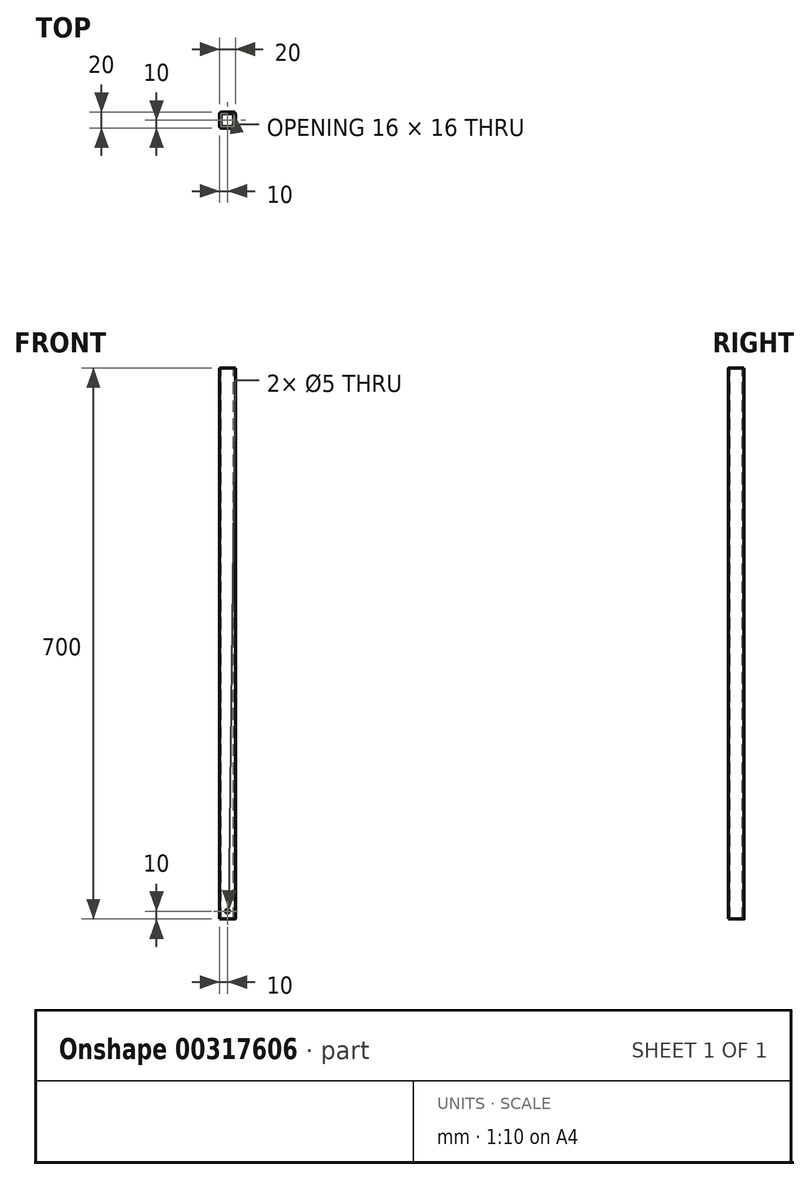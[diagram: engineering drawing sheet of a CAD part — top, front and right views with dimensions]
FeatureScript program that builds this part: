
annotation { "Feature Type Name" : "Feature", "Feature Type Description" : "" }
export const myFeature = defineFeature(function(context is Context, id is Id, definition is map)
    precondition{}
    {
        {
            var Q0;
            Q0=qCreatedBy(makeId("Top.planeOp"),FACE);
            var sketch = newSketch(context, id + "F0", { "sketchPlane" : qUnion([Q0])});
            skLineSegment(sketch, "E0.bottom", {"start": v(10, -10) * mm, "end": v(-10, -10) * mm});
            skLineSegment(sketch, "E0.top", {"start": v(10, 10) * mm, "end": v(-10, 10) * mm});
            skLineSegment(sketch, "E0.left", {"start": v(10, -10) * mm, "end": v(10, 10) * mm});
            skLineSegment(sketch, "E0.right", {"start": v(-10, -10) * mm, "end": v(-10, 10) * mm});
            skSolve(sketch);
        }
        {
            var Q0;
            Q0=makeQuery(id+"F0.imprint","IMPRINT",FACE,{"disambiguationData":[TD([[makeQuery(id+"F0.imprint","IMPRINT",EDGE,{"derivedFrom":sQuery(id+"F0.wireOp",EDGE,"E0.bottom")}),-1.0]])]});
            extrude(context, id + "F1", {"entities" : qUnion([Q0]), "depth" : 700 * mm});
        }
        {
            var Q0;
            Q0=makeQuery(id+"F1.opExtrude","SWEPT_EDGE",EDGE,{"disambiguationData":[OSD([sQuery(id+"F0.wireOp",EDGE,"E0.top"),sQuery(id+"F0.wireOp",EDGE,"E0.right")])]});
            var Q1;
            Q1=makeQuery(id+"F1.opExtrude","SWEPT_EDGE",EDGE,{"disambiguationData":[OSD([sQuery(id+"F0.wireOp",EDGE,"E0.bottom"),sQuery(id+"F0.wireOp",EDGE,"E0.right")])]});
            var Q2;
            Q2=makeQuery(id+"F1.opExtrude","SWEPT_EDGE",EDGE,{"disambiguationData":[OSD([sQuery(id+"F0.wireOp",EDGE,"E0.bottom"),sQuery(id+"F0.wireOp",EDGE,"E0.left")])]});
            var Q3;
            Q3=makeQuery(id+"F1.opExtrude","SWEPT_EDGE",EDGE,{"disambiguationData":[OSD([sQuery(id+"F0.wireOp",EDGE,"E0.top"),sQuery(id+"F0.wireOp",EDGE,"E0.left")])]});
            fillet(context, id + "F2", {"entities" : qUnion([Q0, Q1, Q2, Q3]), "radius" : 2 * mm, "tangentPropagation" : true, "allowEdgeOverflow" : false});
        }
        {
            var Q0;
            Q0=makeQuery(id+"F1.opExtrude","CAP_FACE",FACE,{"disambiguationData":[OSD([sQuery(id+"F0.wireOp",EDGE,"E0.bottom"),sQuery(id+"F0.wireOp",EDGE,"E0.top"),sQuery(id+"F0.wireOp",EDGE,"E0.left"),sQuery(id+"F0.wireOp",EDGE,"E0.right")])],"isStart":false});
            var Q1;
            Q1=makeQuery(id+"F1.opExtrude","CAP_FACE",FACE,{"disambiguationData":[OSD([sQuery(id+"F0.wireOp",EDGE,"E0.bottom"),sQuery(id+"F0.wireOp",EDGE,"E0.top"),sQuery(id+"F0.wireOp",EDGE,"E0.left"),sQuery(id+"F0.wireOp",EDGE,"E0.right")])],"isStart":true});
            shell(context, id + "F3", {"entities" : qUnion([Q0, Q1]), "thickness" : 2 * mm});
        }
        {
            var Q0;
            Q0=makeQuery(id+"F3.opShell","OFFSET_EDGE",EDGE,{"disambiguationData":[OSD([sQuery(id+"F0.wireOp",EDGE,"E0.top"),sQuery(id+"F0.wireOp",EDGE,"E0.left")])]});
            var Q1;
            Q1=makeQuery(id+"F3.opShell","OFFSET_EDGE",EDGE,{"disambiguationData":[OSD([sQuery(id+"F0.wireOp",EDGE,"E0.bottom"),sQuery(id+"F0.wireOp",EDGE,"E0.left")])]});
            var Q2;
            Q2=makeQuery(id+"F3.opShell","OFFSET_EDGE",EDGE,{"disambiguationData":[OSD([sQuery(id+"F0.wireOp",EDGE,"E0.bottom"),sQuery(id+"F0.wireOp",EDGE,"E0.right")])]});
            var Q3;
            Q3=makeQuery(id+"F3.opShell","OFFSET_EDGE",EDGE,{"disambiguationData":[OSD([sQuery(id+"F0.wireOp",EDGE,"E0.top"),sQuery(id+"F0.wireOp",EDGE,"E0.right")])]});
            fillet(context, id + "F4", {"entities" : qUnion([Q0, Q1, Q2, Q3]), "radius" : 2 * mm, "tangentPropagation" : true, "allowEdgeOverflow" : false});
        }
        {
            var Q0;
            Q0=makeQuery(id+"F1.opExtrude","SWEPT_FACE",FACE,{"disambiguationData":[OSD([sQuery(id+"F0.wireOp",EDGE,"E0.top")])]});
            var sketch = newSketch(context, id + "F5", { "sketchPlane" : qUnion([Q0])});
            skCircle(sketch, "E1", {"center": v(0, 10) * mm, "radius": 2.5 * mm});
            skSolve(sketch);
        }
        {
            var Q0;
            Q0=makeQuery(id+"F5.imprint","IMPRINT",FACE,{"disambiguationData":[TD([[makeQuery(id+"F5.imprint","IMPRINT",EDGE,{"derivedFrom":sQuery(id+"F5.wireOp",EDGE,"E1")}),1.0]])]});
            extrude(context, id + "F6", {"entities" : qUnion([Q0]), "operationType" : NewBodyOperationType.REMOVE, "oppositeDirection" : true, "depth" : 25.2 * mm});
        }
    });
